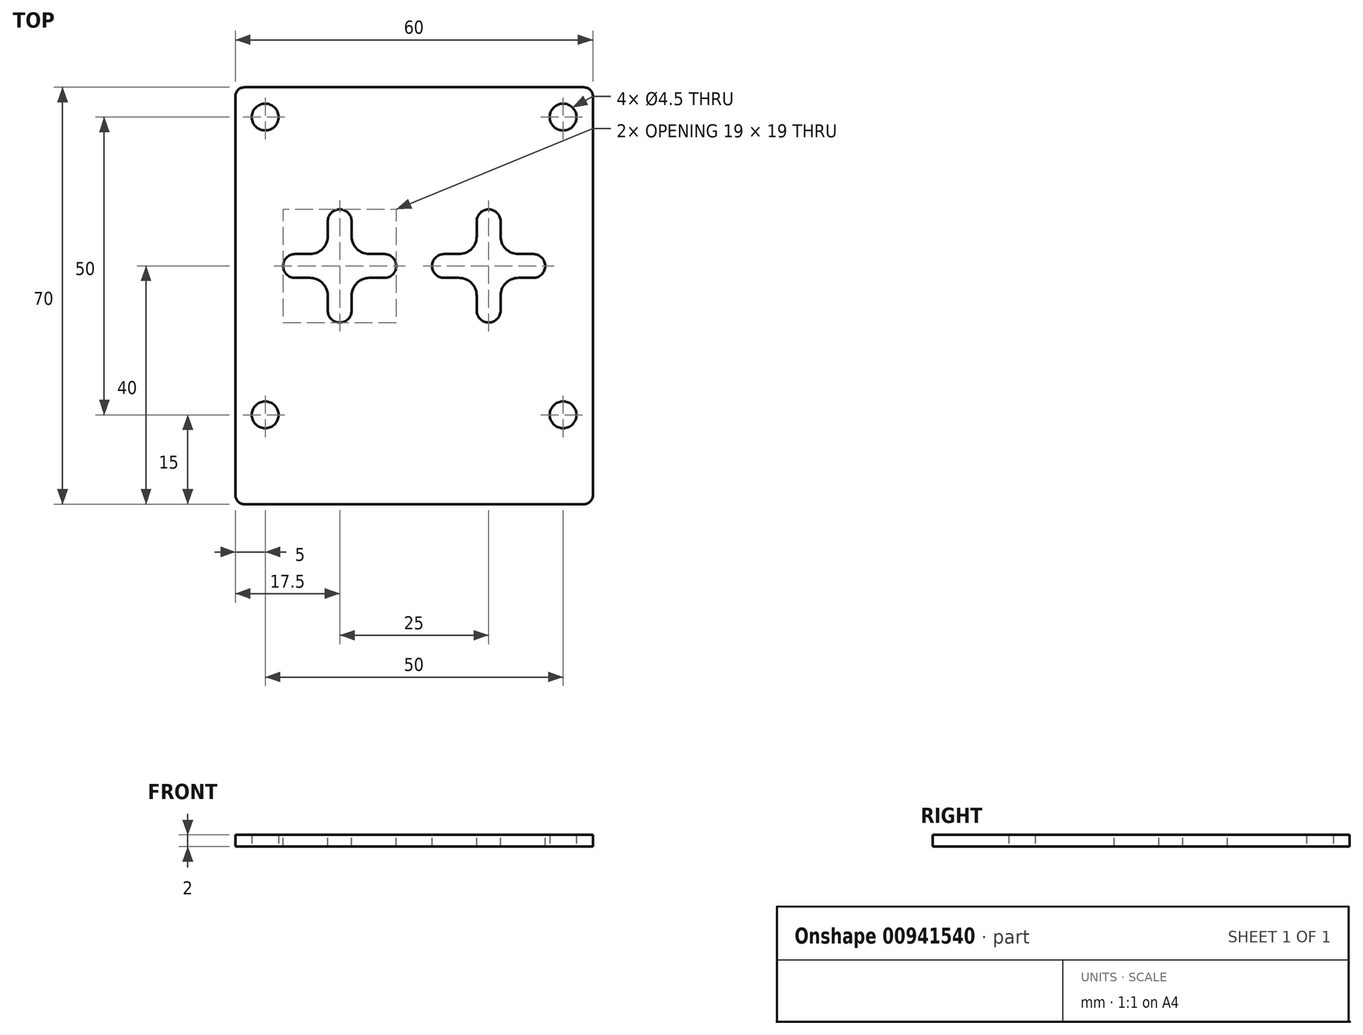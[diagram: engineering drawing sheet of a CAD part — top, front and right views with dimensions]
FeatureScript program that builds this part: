
annotation { "Feature Type Name" : "Feature", "Feature Type Description" : "" }
export const myFeature = defineFeature(function(context is Context, id is Id, definition is map)
    precondition{}
    {
        {
            var Q0;
            Q0=qCreatedBy(makeId("Top.planeOp"),FACE);
            var sketch = newSketch(context, id + "F0", { "sketchPlane" : qUnion([Q0])});
            skLineSegment(sketch, "E0.bottom", {"start": v(-30, 35) * mm, "end": v(30, 35) * mm});
            skLineSegment(sketch, "E0.top", {"start": v(-30, -35) * mm, "end": v(30, -35) * mm});
            skLineSegment(sketch, "E0.left", {"start": v(-30, 35) * mm, "end": v(-30, -35) * mm});
            skLineSegment(sketch, "E0.right", {"start": v(30, 35) * mm, "end": v(30, -35) * mm});
            skPoint(sketch, "E0.middle", {"position": v(0, 0) * mm});
            skLineSegment(sketch, "E1.bottom", {"start": v(-25, 30) * mm, "end": v(25, 30) * mm});
            skLineSegment(sketch, "E1.top", {"start": v(-25, -20) * mm, "end": v(25, -20) * mm});
            skLineSegment(sketch, "E1.left", {"start": v(-25, 30) * mm, "end": v(-25, -20) * mm});
            skLineSegment(sketch, "E1.right", {"start": v(25, 30) * mm, "end": v(25, -20) * mm});
            skCircle(sketch, "E2", {"center": v(-25, 30) * mm, "radius": 2.25 * mm});
            skCircle(sketch, "E3", {"center": v(25, 30) * mm, "radius": 2.25 * mm});
            skCircle(sketch, "E4", {"center": v(-25, -20) * mm, "radius": 2.25 * mm});
            skCircle(sketch, "E5", {"center": v(25, -20) * mm, "radius": 2.25 * mm});
            skSolve(sketch);
        }
        {
            var Q0;
            Q0=makeQuery(id+"F0.imprint","IMPRINT",FACE,{"disambiguationData":[TD([[makeQuery(id+"F0.imprint","IMPRINT",EDGE,{"derivedFrom":sQuery(id+"F0.wireOp",EDGE,"E0.bottom")}),-1.0]])]});
            var Q1;
            {var subQ5=sQuery(id+"F0.wireOp",EDGE,"E2");var subQ13=sQuery(id+"F0.wireOp",EDGE,"E1.bottom");var subQ14=makeQuery(id+"F0.imprint","INTERSECT",VERTEX,{"derivedFrom":[subQ13,subQ5]});Q1=makeQuery(id+"F0.imprint","IMPRINT",FACE,{"disambiguationData":[TD([[makeQuery(id+"F0.imprint","IMPRINT",EDGE,{"disambiguationData":[TD([[subQ14,-1.0]])],"derivedFrom":subQ13}),-1.0]])]});}
            extrude(context, id + "F1", {"entities" : qUnion([Q0, Q1]), "depth" : 2 * mm, "offsetDistance" : 25 * mm});
        }
        {
            var Q0;
            Q0=makeQuery(id+"F1.opExtrude","SWEPT_EDGE",EDGE,{"disambiguationData":[OSD([sQuery(id+"F0.wireOp",EDGE,"E0.bottom"),sQuery(id+"F0.wireOp",EDGE,"E0.left")])]});
            var Q1;
            Q1=makeQuery(id+"F1.opExtrude","SWEPT_EDGE",EDGE,{"disambiguationData":[OSD([sQuery(id+"F0.wireOp",EDGE,"E0.bottom"),sQuery(id+"F0.wireOp",EDGE,"E0.right")])]});
            var Q2;
            Q2=makeQuery(id+"F1.opExtrude","SWEPT_EDGE",EDGE,{"disambiguationData":[OSD([sQuery(id+"F0.wireOp",EDGE,"E0.top"),sQuery(id+"F0.wireOp",EDGE,"E0.left")])]});
            var Q3;
            Q3=makeQuery(id+"F1.opExtrude","SWEPT_EDGE",EDGE,{"disambiguationData":[OSD([sQuery(id+"F0.wireOp",EDGE,"E0.top"),sQuery(id+"F0.wireOp",EDGE,"E0.right")])]});
            fillet(context, id + "F2", {"entities" : qUnion([Q0, Q1, Q2, Q3]), "radius" : 1.5 * mm, "tangentPropagation" : true, "allowEdgeOverflow" : false});
        }
        {
            var Q0;
            Q0=makeQuery(id+"F1.opExtrude","CAP_FACE",FACE,{"disambiguationData":[OSD([sQuery(id+"F0.wireOp",EDGE,"E0.bottom"),sQuery(id+"F0.wireOp",EDGE,"E0.top"),sQuery(id+"F0.wireOp",EDGE,"E0.left"),sQuery(id+"F0.wireOp",EDGE,"E0.right"),sQuery(id+"F0.wireOp",EDGE,"E2"),sQuery(id+"F0.wireOp",EDGE,"E3"),sQuery(id+"F0.wireOp",EDGE,"E4"),sQuery(id+"F0.wireOp",EDGE,"E5")])],"isStart":false});
            var sketch = newSketch(context, id + "F3", { "sketchPlane" : qUnion([Q0])});
            skLineSegment(sketch, "E6", {"start": v(-12.5, 12.5) * mm, "end": v(-12.5, -2.5) * mm});
            skLineSegment(sketch, "E7", {"start": v(-20, 5) * mm, "end": v(-5, 5) * mm});
            skArc(sketch, "E8.0.startCap", {"start": v(-20, 3) * mm, "mid": v(-22, 5) * mm, "end": v(-20, 7) * mm});
            skArc(sketch, "E8.0.endCap", {"start": v(-5, 7) * mm, "mid": v(-3, 5) * mm, "end": v(-5, 3) * mm});
            skLineSegment(sketch, "E8.0.left", {"start": v(-20, 7) * mm, "end": v(-5, 7) * mm});
            skLineSegment(sketch, "E8.0.right", {"start": v(-20, 3) * mm, "end": v(-5, 3) * mm});
            skArc(sketch, "E9.0.startCap", {"start": v(-14.5, 12.5) * mm, "mid": v(-12.5, 14.5) * mm, "end": v(-10.5, 12.5) * mm});
            skArc(sketch, "E9.0.endCap", {"start": v(-10.5, -2.5) * mm, "mid": v(-12.5, -4.5) * mm, "end": v(-14.5, -2.5) * mm});
            skLineSegment(sketch, "E9.0.left", {"start": v(-10.5, 12.5) * mm, "end": v(-10.5, -2.5) * mm});
            skLineSegment(sketch, "E9.0.right", {"start": v(-14.5, 12.5) * mm, "end": v(-14.5, -2.5) * mm});
            skLineSegment(sketch, "E10.1.0.0", {"start": v(5, 3) * mm, "end": v(20, 3) * mm});
            skLineSegment(sketch, "E10.1.0.1", {"start": v(5, 5) * mm, "end": v(20, 5) * mm});
            skArc(sketch, "E10.1.0.2", {"start": v(5, 3) * mm, "mid": v(3, 5) * mm, "end": v(5, 7) * mm});
            skLineSegment(sketch, "E10.1.0.3", {"start": v(5, 7) * mm, "end": v(20, 7) * mm});
            skLineSegment(sketch, "E10.1.0.4", {"start": v(14.5, 12.5) * mm, "end": v(14.5, -2.5) * mm});
            skLineSegment(sketch, "E10.1.0.5", {"start": v(10.5, 12.5) * mm, "end": v(10.5, -2.5) * mm});
            skArc(sketch, "E10.1.0.6", {"start": v(20, 7) * mm, "mid": v(22, 5) * mm, "end": v(20, 3) * mm});
            skLineSegment(sketch, "E10.1.0.7", {"start": v(12.5, 12.5) * mm, "end": v(12.5, -2.5) * mm});
            skArc(sketch, "E10.1.0.8", {"start": v(10.5, 12.5) * mm, "mid": v(12.5, 14.5) * mm, "end": v(14.5, 12.5) * mm});
            skArc(sketch, "E10.1.0.9", {"start": v(14.5, -2.5) * mm, "mid": v(12.5, -4.5) * mm, "end": v(10.5, -2.5) * mm});
            skLineSegment(sketch, "E10.direction1", {"start": v(-14.5, -2.5) * mm, "end": v(10.5, -2.5) * mm, "construction": true});
            skSolve(sketch);
        }
        {
            var Q0;
            Q0 = qSketchRegion(id + "F3", true);
            extrude(context, id + "F4", {"entities" : qUnion([Q0]), "operationType" : NewBodyOperationType.REMOVE, "oppositeDirection" : true, "depth" : 2 * mm, "offsetDistance" : 25 * mm});
        }
        {
            var Q0;
            Q0=makeQuery(id+"F4.boolean.opBoolean","COPY",EDGE,{"derivedFrom":makeQuery(id+"F4.opExtrude","SWEPT_EDGE",EDGE,{"disambiguationData":[OSD([sQuery(id+"F3.wireOp",EDGE,"E8.0.right"),sQuery(id+"F3.wireOp",EDGE,"E9.0.right")])]})});
            var Q1;
            Q1=makeQuery(id+"F4.boolean.opBoolean","COPY",EDGE,{"derivedFrom":makeQuery(id+"F4.opExtrude","SWEPT_EDGE",EDGE,{"disambiguationData":[OSD([sQuery(id+"F3.wireOp",EDGE,"E8.0.right"),sQuery(id+"F3.wireOp",EDGE,"E9.0.left")])]})});
            var Q2;
            Q2=makeQuery(id+"F4.boolean.opBoolean","COPY",EDGE,{"derivedFrom":makeQuery(id+"F4.opExtrude","SWEPT_EDGE",EDGE,{"disambiguationData":[OSD([sQuery(id+"F3.wireOp",EDGE,"E8.0.left"),sQuery(id+"F3.wireOp",EDGE,"E9.0.right")])]})});
            var Q3;
            Q3=makeQuery(id+"F4.boolean.opBoolean","COPY",EDGE,{"derivedFrom":makeQuery(id+"F4.opExtrude","SWEPT_EDGE",EDGE,{"disambiguationData":[OSD([sQuery(id+"F3.wireOp",EDGE,"E8.0.left"),sQuery(id+"F3.wireOp",EDGE,"E9.0.left")])]})});
            var Q4;
            Q4=makeQuery(id+"F4.boolean.opBoolean","COPY",EDGE,{"derivedFrom":makeQuery(id+"F4.opExtrude","SWEPT_EDGE",EDGE,{"disambiguationData":[OSD([sQuery(id+"F3.wireOp",EDGE,"E10.1.0.0"),sQuery(id+"F3.wireOp",EDGE,"E10.1.0.5")])]})});
            var Q5;
            Q5=makeQuery(id+"F4.boolean.opBoolean","COPY",EDGE,{"derivedFrom":makeQuery(id+"F4.opExtrude","SWEPT_EDGE",EDGE,{"disambiguationData":[OSD([sQuery(id+"F3.wireOp",EDGE,"E10.1.0.3"),sQuery(id+"F3.wireOp",EDGE,"E10.1.0.5")])]})});
            var Q6;
            Q6=makeQuery(id+"F4.boolean.opBoolean","COPY",EDGE,{"derivedFrom":makeQuery(id+"F4.opExtrude","SWEPT_EDGE",EDGE,{"disambiguationData":[OSD([sQuery(id+"F3.wireOp",EDGE,"E10.1.0.0"),sQuery(id+"F3.wireOp",EDGE,"E10.1.0.4")])]})});
            var Q7;
            Q7=makeQuery(id+"F4.boolean.opBoolean","COPY",EDGE,{"derivedFrom":makeQuery(id+"F4.opExtrude","SWEPT_EDGE",EDGE,{"disambiguationData":[OSD([sQuery(id+"F3.wireOp",EDGE,"E10.1.0.3"),sQuery(id+"F3.wireOp",EDGE,"E10.1.0.4")])]})});
            fillet(context, id + "F5", {"entities" : qUnion([Q0, Q1, Q2, Q3, Q4, Q5, Q6, Q7]), "radius" : 3 * mm, "tangentPropagation" : true, "allowEdgeOverflow" : false});
        }
    });
